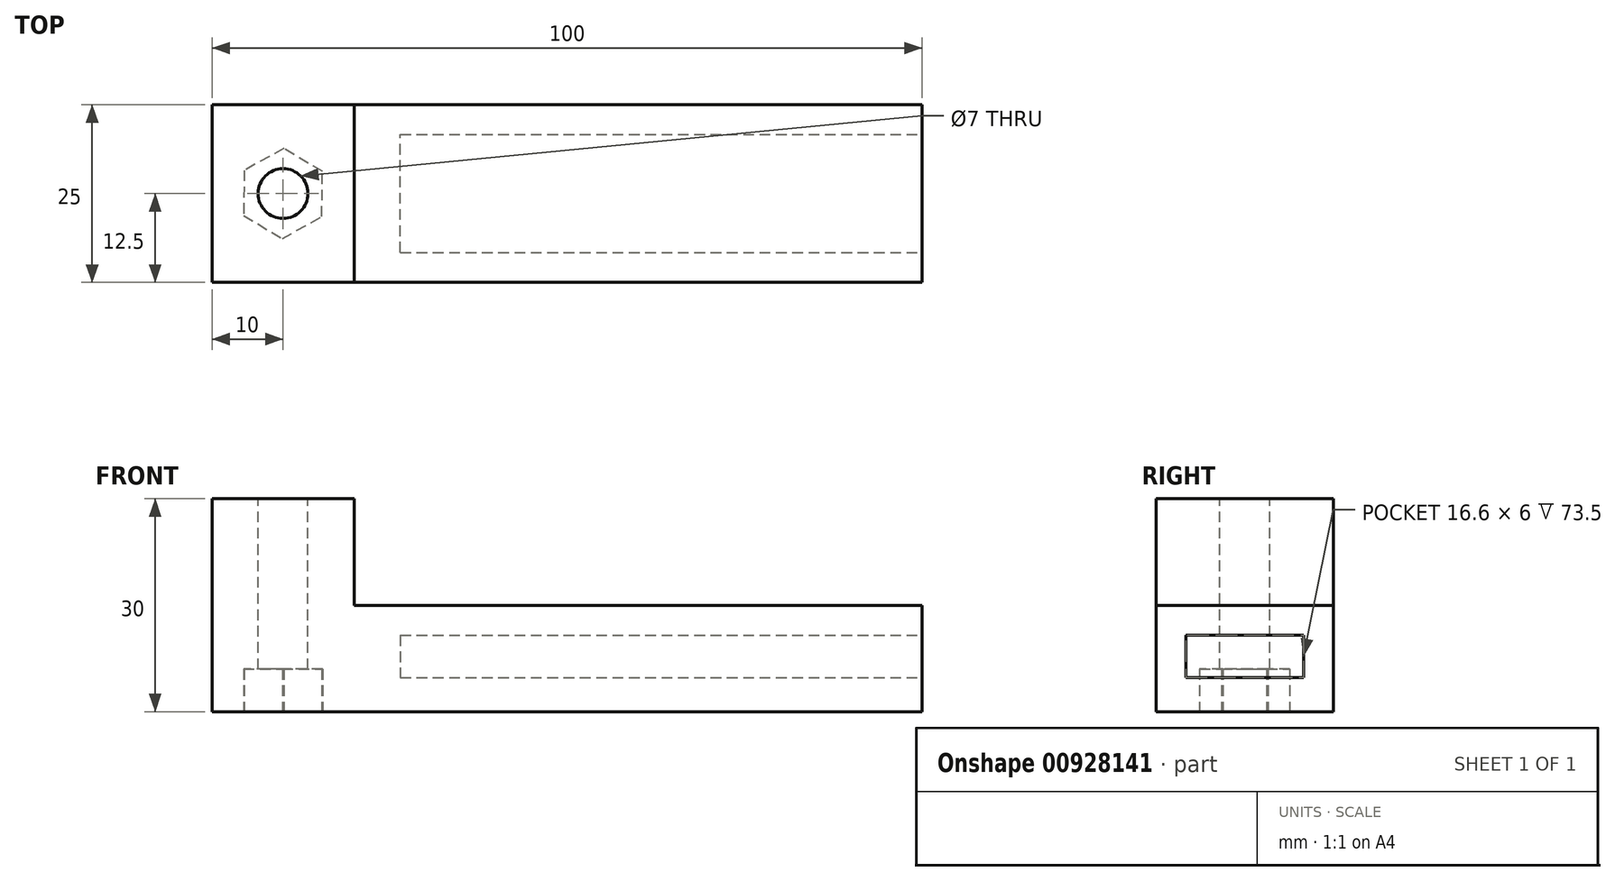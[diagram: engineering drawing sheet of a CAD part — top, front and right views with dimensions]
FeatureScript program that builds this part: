
annotation { "Feature Type Name" : "Feature", "Feature Type Description" : "" }
export const myFeature = defineFeature(function(context is Context, id is Id, definition is map)
    precondition{}
    {
        {
            var Q0;
            Q0=qCreatedBy(makeId("Top.planeOp"),FACE);
            var sketch = newSketch(context, id + "F0", { "sketchPlane" : qUnion([Q0])});
            skLineSegment(sketch, "E0.bottom", {"start": v(50, 12.5) * mm, "end": v(-50, 12.5) * mm});
            skLineSegment(sketch, "E0.top", {"start": v(50, -12.5) * mm, "end": v(-50, -12.5) * mm});
            skLineSegment(sketch, "E0.left", {"start": v(50, 12.5) * mm, "end": v(50, -12.5) * mm});
            skLineSegment(sketch, "E0.right", {"start": v(-50, 12.5) * mm, "end": v(-50, -12.5) * mm});
            skPoint(sketch, "E0.middle", {"position": v(0, 0) * mm});
            skSolve(sketch);
        }
        {
            var Q0;
            Q0=makeQuery(id+"F0.imprint","IMPRINT",FACE,{"disambiguationData":[TD([[makeQuery(id+"F0.imprint","IMPRINT",EDGE,{"derivedFrom":sQuery(id+"F0.wireOp",EDGE,"E0.bottom")}),1.0]])]});
            extrude(context, id + "F1", {"entities" : qUnion([Q0]), "depth" : 15 * mm, "offsetDistance" : 25 * mm});
        }
        {
            var Q0;
            Q0=makeQuery(id+"F1.opExtrude","SWEPT_FACE",FACE,{"disambiguationData":[OSD([sQuery(id+"F0.wireOp",EDGE,"E0.left")])]});
            var sketch = newSketch(context, id + "F2", { "sketchPlane" : qUnion([Q0])});
            skLineSegment(sketch, "E1.bottom", {"start": v(-8.3, 10.79) * mm, "end": v(8.3, 10.79) * mm});
            skLineSegment(sketch, "E1.top", {"start": v(-8.3, 4.79) * mm, "end": v(8.3, 4.79) * mm});
            skLineSegment(sketch, "E1.left", {"start": v(-8.3, 10.79) * mm, "end": v(-8.3, 4.79) * mm});
            skLineSegment(sketch, "E1.right", {"start": v(8.3, 10.79) * mm, "end": v(8.3, 4.79) * mm});
            skSolve(sketch);
        }
        {
            var Q0;
            Q0=makeQuery(id+"F2.imprint","IMPRINT",FACE,{"disambiguationData":[TD([[makeQuery(id+"F2.imprint","IMPRINT",EDGE,{"derivedFrom":sQuery(id+"F2.wireOp",EDGE,"E1.bottom")}),-1.0]])]});
            extrude(context, id + "F3", {"entities" : qUnion([Q0]), "operationType" : NewBodyOperationType.REMOVE, "oppositeDirection" : true, "depth" : 73.5 * mm, "offsetDistance" : 25 * mm});
        }
        {
            var Q0;
            Q0=makeQuery(id+"F1.opExtrude","CAP_FACE",FACE,{"disambiguationData":[OSD([sQuery(id+"F0.wireOp",EDGE,"E0.bottom"),sQuery(id+"F0.wireOp",EDGE,"E0.top"),sQuery(id+"F0.wireOp",EDGE,"E0.left"),sQuery(id+"F0.wireOp",EDGE,"E0.right")])],"isStart":false});
            var sketch = newSketch(context, id + "F4", { "sketchPlane" : qUnion([Q0])});
            skLineSegment(sketch, "E2.bottom", {"start": v(-50, -12.5) * mm, "end": v(-30, -12.5) * mm});
            skLineSegment(sketch, "E2.top", {"start": v(-50, 12.5) * mm, "end": v(-30, 12.5) * mm});
            skLineSegment(sketch, "E2.left", {"start": v(-50, -12.5) * mm, "end": v(-50, 12.5) * mm});
            skLineSegment(sketch, "E2.right", {"start": v(-30, -12.5) * mm, "end": v(-30, 12.5) * mm});
            skSolve(sketch);
        }
        {
            var Q0;
            Q0=makeQuery(id+"F4.imprint","IMPRINT",FACE,{"disambiguationData":[TD([[makeQuery(id+"F4.imprint","IMPRINT",EDGE,{"derivedFrom":sQuery(id+"F4.wireOp",EDGE,"E2.bottom")}),-1.0]])]});
            extrude(context, id + "F5", {"entities" : qUnion([Q0]), "operationType" : NewBodyOperationType.ADD, "depth" : 15 * mm, "offsetDistance" : 25 * mm});
        }
        {
            var Q0;
            Q0=makeQuery(id+"F5.opExtrude","CAP_FACE",FACE,{"disambiguationData":[OSD([sQuery(id+"F4.wireOp",EDGE,"E2.bottom"),sQuery(id+"F4.wireOp",EDGE,"E2.top"),sQuery(id+"F4.wireOp",EDGE,"E2.left"),sQuery(id+"F4.wireOp",EDGE,"E2.right")])],"isStart":false});
            var sketch = newSketch(context, id + "F6", { "sketchPlane" : qUnion([Q0])});
            skCircle(sketch, "E3", {"center": v(-40, 0) * mm, "radius": 3.5 * mm});
            skSolve(sketch);
        }
        {
            var Q0;
            Q0=makeQuery(id+"F6.imprint","IMPRINT",FACE,{"disambiguationData":[TD([[makeQuery(id+"F6.imprint","IMPRINT",EDGE,{"derivedFrom":sQuery(id+"F6.wireOp",EDGE,"E3")}),1.0]])]});
            extrude(context, id + "F7", {"entities" : qUnion([Q0]), "operationType" : NewBodyOperationType.REMOVE, "endBound" : BoundingType.THROUGH_ALL, "oppositeDirection" : true, "depth" : 20 * mm, "offsetDistance" : 25 * mm});
        }
        {
            var Q0;
            Q0=makeQuery(id+"F1.opExtrude","CAP_FACE",FACE,{"disambiguationData":[OSD([sQuery(id+"F0.wireOp",EDGE,"E0.bottom"),sQuery(id+"F0.wireOp",EDGE,"E0.top"),sQuery(id+"F0.wireOp",EDGE,"E0.left"),sQuery(id+"F0.wireOp",EDGE,"E0.right")])],"isStart":true});
            var sketch = newSketch(context, id + "F8", { "sketchPlane" : qUnion([Q0])});
            skPoint(sketch, "E4.1", {"position": v(-40, 0) * mm});
            skCircle(sketch, "E5.cCircle", {"center": v(-40, 0) * mm, "radius": 5.5 * mm, "construction": true});
            skLineSegment(sketch, "E5.0", {"start": v(-45.55, 3.1) * mm, "end": v(-40.1, 6.35) * mm});
            skLineSegment(sketch, "E5.1", {"start": v(-40.1, 6.35) * mm, "end": v(-34.55, 3.26) * mm});
            skLineSegment(sketch, "E5.2", {"start": v(-34.55, 3.26) * mm, "end": v(-34.45, -3.1) * mm});
            skLineSegment(sketch, "E5.3", {"start": v(-34.45, -3.1) * mm, "end": v(-39.9, -6.35) * mm});
            skLineSegment(sketch, "E5.4", {"start": v(-39.9, -6.35) * mm, "end": v(-45.45, -3.26) * mm});
            skLineSegment(sketch, "E5.5", {"start": v(-45.45, -3.26) * mm, "end": v(-45.55, 3.1) * mm});
            skPoint(sketch, "E5.0.midPoint", {"position": v(-42.82, 4.72) * mm});
            skSolve(sketch);
        }
        {
            var Q0;
            Q0=makeQuery(id+"F8.imprint","IMPRINT",FACE,{"disambiguationData":[TD([[makeQuery(id+"F8.imprint","IMPRINT",EDGE,{"derivedFrom":sQuery(id+"F8.wireOp",EDGE,"E5.0")}),-1.0]])]});
            extrude(context, id + "F9", {"entities" : qUnion([Q0]), "operationType" : NewBodyOperationType.REMOVE, "oppositeDirection" : true, "depth" : 6 * mm, "offsetDistance" : 25 * mm});
        }
    });
